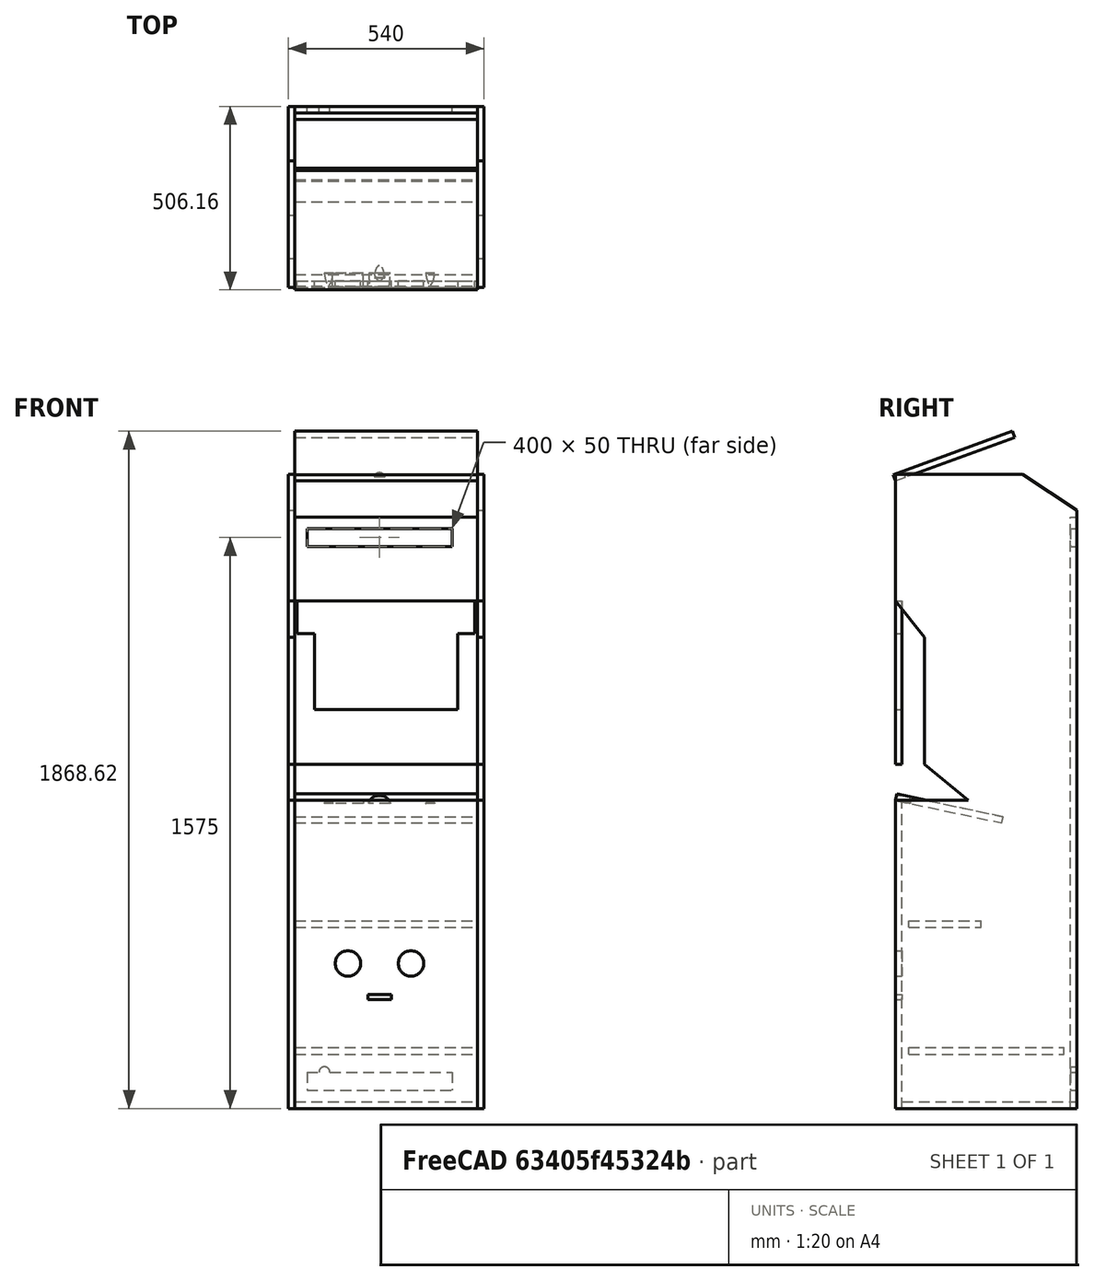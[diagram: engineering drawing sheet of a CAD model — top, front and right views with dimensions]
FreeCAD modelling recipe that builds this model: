
FCSTD DOCUMENT  (FreeCAD 1.0R39319 (Git))
Label: ARTIFACT_Cabinet
License: All rights reserved
LicenseURL: https://en.wikipedia.org/wiki/All_rights_reserved
objects: Part::Box×8, Part::Feature×7
note: 15 computed .brp shape members not serialized (recipe doc carries the construction recipe); baked Part::Feature solids carry a one-line shape summary decoded from their .brp

FEATURE [Part::Feature] Side_Panel_Left
  shape: bbox 18 x 500 x 1750 mm, 13 faces (baked)
FEATURE [Part::Feature] Side_Panel_Right
  Placement = pos=(522,0,0) rot=(0,0,1;0rad)
  shape: bbox 18 x 500 x 1750 mm, 13 faces (baked)
FEATURE [Part::Box] Base_Platform
  AttacherType = Attacher::AttachEngine3D
  Height = 18
  Length = 504
  Placement = pos=(18,18,0) rot=(0,0,1;0rad)
  Width = 464
FEATURE [Part::Box] Front_Panel_Lower
  AttacherType = Attacher::AttachEngine3D
  Height = 850
  Length = 504
  Placement = pos=(18,0,0) rot=(0,0,1;0rad)
  Width = 18
FEATURE [Part::Box] Front_Panel_Screen
  AttacherType = Attacher::AttachEngine3D
  Height = 450
  Length = 504
  Placement = pos=(18,0,950) rot=(0,0,1;0rad)
  Width = 18
FEATURE [Part::Box] Back_Panel
  AttacherType = Attacher::AttachEngine3D
  Height = 1614
  Length = 504
  Placement = pos=(18,482,18) rot=(0,0,1;0rad)
  Width = 18
FEATURE [Part::Box] Control_Panel
  AttacherType = Attacher::AttachEngine3D
  Height = 18
  Length = 504
  Placement = pos=(18,0,850) rot=(1,0,0;-0.20944rad)
  Width = 300
FEATURE [Part::Box] Marquee_Panel
  AttacherType = Attacher::AttachEngine3D
  Height = 18
  Length = 504
  Placement = pos=(18,0,1732) rot=(1,0,0;0.349066rad)
  Width = 350
FEATURE [Part::Box] Shelf_Base
  AttacherType = Attacher::AttachEngine3D
  Height = 18
  Length = 504
  Placement = pos=(18,36,150) rot=(0,0,1;0rad)
  Width = 428
FEATURE [Part::Box] Shelf_Middle
  AttacherType = Attacher::AttachEngine3D
  Height = 18
  Length = 504
  Placement = pos=(18,36,500) rot=(0,0,1;0rad)
  Width = 200
FEATURE [Part::Feature] Front_Panel_Lower_Cut
  shape: bbox 504 x 18 x 850 mm, 12 faces (baked)
FEATURE [Part::Feature] Front_Panel_Screen_Cut
  shape: bbox 504 x 18 x 450 mm, 14 faces (baked)
FEATURE [Part::Feature] Control_Panel_Cut
  shape: bbox 504 x 297.2 x 79.98 mm, 20 faces (baked)
FEATURE [Part::Feature] Back_Panel_Cut
  shape: bbox 504 x 18 x 1614 mm, 17 faces (baked)
FEATURE [Part::Feature] Marquee_Panel_Cut
  shape: bbox 504 x 335 x 136.6 mm, 9 faces (baked)
